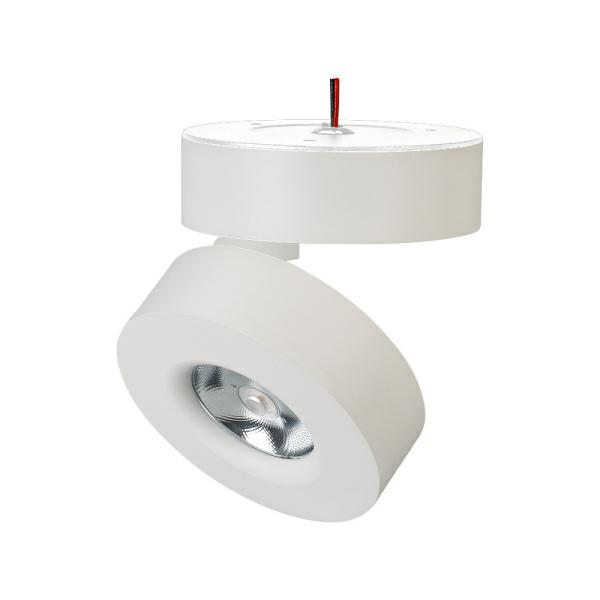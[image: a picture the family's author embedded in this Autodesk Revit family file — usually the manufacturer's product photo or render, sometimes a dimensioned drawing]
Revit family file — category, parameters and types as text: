
# Revit family: MONA-SURFACE
name_source: partatom
category: Осветительные приборы
revit_build: Autodesk Revit 2017 (Build: 20160225_1515(x64)
units: mm (PartAtom-declared; Revit-internal decimal feet)

## family parameters
Всегда вертикально = Да
Источник света = Нет
На основе рабочей плоскости = Нет
Общий = Нет
При загрузке вырезать с полостями = Нет
Размер круглого соединителя = Использовать диаметр
Тип детали = Нормальный
Точка расчета площади = Нет

## types (6) — shared parameters
ADSK_Единица измерения = шт.
ADSK_Завод-изготовитель = ARLIGHT
ADSK_Классификация нагрузок = Освещение
ADSK_Количество фаз = 1
ADSK_Количество фаз числовое = 1
ADSK_Коэффициент мощности = 0.53
ADSK_Масса_Текст = 0.674
ADSK_Наименование = Светильник
ADSK_Напряжение = 230 В
ADSK_Номинальная мощность = 12 Вт
ADSK_Полная мощность = 23 В·А
ADSK_Размер_Высота = 71 мм
ADSK_Размер_Диаметр = 100 мм
ADSK_Ток = 0 А
ARL_Драйвер = Встроенный (DC 300mA, 25-42V)
ARL_Индекс цветопередачи = >90
ARL_Класс защиты от поражения электрическим током = II
ARL_Класс пылевлагозащиты = IP40
ARL_Область использования = Для освещения в квартирах, офисах, музеях, магазинах с высокими требованиями к качеству света
ARL_Рабочая температура окружающей среды = -10...+50 °C
ARL_Серия = MONA
ARL_Способ монтажа = Накладной
ARL_Тип товара = Светильник
ARL_Угол обзора = 24°
URL = https://arlight.ru
Группа модели = Светильники
Изготовитель = ARLIGHT
Изготовитель (сайт) = www.arlight.ru
Изготовитель (телефон) = 8 800 505 26 29
Исходная интенсивность (лм) = 800
Полная установленная мощность = 23 В·А
Разработчик = НТЦ Конструктор
Разработчик (URL) = https://constructor.ru
Разработчик (телефон) = +7 (495) 781-05-35

## per-type parameters (varying)
| type | ADSK_Код изделия | ADSK_Марка | ARL_Материал корпуса | ARL_Обозначение корпуса | ARL_Цвет покрытия | ARL_Цвет свечения | Комментарии к типоразмеру | Описание | Фотометрия | Цветовая температура (К) |
| 025438 Светильник SP-MONA-SURFACE-R100-12W White5000 (WH, 24 deg) | Арт. 025438 | SP-MONA-SURFACE-R100-12W White5000 | Металл, белый | Корпус круглый, алюминий, цвет белый | Белый | Дневной 5000K | Арт. 025438 | Накладной откидной поворотный светильник 12 Вт. Цвет БЕЛЫЙ 5000K, св.поток 800лм, CRI(Ra)>90, угол свечения 24°, угол поворота 355°, угол наклона 90°. Корпус круглый, белый алюминий, IP40. Размер DxH Ø100x71 мм. Питание AC 220-240V, 12 Вт, драйвер встроенный (DC 300mA, 25-42V) | MONA-SURFACE IES Data : 025438_SP-MONA-SURFACE-R100-12W White5000 (WH, 24 deg) | 5000 |
| 025439 Светильник SP-MONA-SURFACE-R100-12W Day4000 (WH, 24 deg) | Арт. 025439 | SP-MONA-SURFACE-R100-12W Day4000 | Металл, белый | Корпус круглый, алюминий, цвет белый | Белый | Дневной 4000K | Арт. 025439 | Накладной откидной поворотный светильник 12 Вт. Цвет ДНЕВНОЙ 4000K, св.поток 800лм, CRI(Ra)>90, угол свечения 24°, угол поворота 355°, угол наклона 90°. Корпус круглый, белый алюминий, IP40. Размер DxH Ø100x71 мм. Питание AC 220-240V, 12 Вт, драйвер встроенный (DC 300mA, 25-42V) | MONA-SURFACE IES Data : 025439_SP-MONA-SURFACE-R100-12W Day4000 (WH, 24 deg) | 4000 |
| 025440 Светильник SP-MONA-SURFACE-R100-12W Warm3000 (WH, 24 deg) | Арт. 025440 | SP-MONA-SURFACE-R100-12W Warm3000 | Металл, белый | Корпус круглый, алюминий, цвет белый | Белый | Теплый 3000K | Арт. 025440 | Накладной откидной поворотный светильник 12 Вт. Цвет ТЕПЛЫЙ 3000K, св.поток 800лм, CRI(Ra)>90, угол свечения 24°, угол поворота 355°, угол наклона 90°. Корпус круглый, белый алюминий, IP40. Размер DxH Ø100x71 мм. Питание AC 220-240V, 12 Вт, драйвер встроенный (DC 300mA, 25-42V) | MONA-SURFACE IES Data : 025440_SP-MONA-SURFACE-R100-12W Warm3000 (WH, 24 deg) | 3000 |
| 025441 Светильник SP-MONA-SURFACE-R100-12W White5000 (BK, 24 deg) | Арт. 025441 | SP-MONA-SURFACE-R100-12W White5000 | Металл, чёрный | Корпус круглый, алюминий, цвет черный | Черный | Дневной 5000K | Арт. 025441 | Накладной откидной поворотный светильник 12 Вт. Цвет БЕЛЫЙ 5000K, св.поток 800лм, CRI(Ra)>90, угол свечения 24°, угол поворота 355°, угол наклона 90°. Корпус круглый, черный алюминий, IP40. Размер DxH Ø100x71 мм. Питание AC 220-240V, 12 Вт, драйвер встроенный (DC 300mA, 25-42V) | MONA-SURFACE IES Data : 025441_SP-MONA-SURFACE-R100-12W White5000 (BK, 24 deg) | 5000 |
| 025442 Светильник SP-MONA-SURFACE-R100-12W Day4000 (BK, 24 deg) | Арт. 025442 | SP-MONA-SURFACE-R100-12W Day4000 | Металл, чёрный | Корпус круглый, алюминий, цвет черный | Черный | Дневной 4000K | Арт. 025442 | Накладной откидной поворотный светильник 12 Вт. Цвет ДНЕВНОЙ 4000K, св.поток 800лм, CRI(Ra)>90, угол свечения 24°, угол поворота 355°, угол наклона 90°. Корпус круглый, черный алюминий, IP40. Размер DxH Ø100x71 мм. Питание AC 220-240V, 12 Вт, драйвер встроенный (DC 300mA, 25-42V) | MONA-SURFACE IES Data : 025442_SP-MONA-SURFACE-R100-12W Day4000 (BK, 24 deg) | 4000 |
| 025443 Светильник SP-MONA-SURFACE-R100-12W Warm3000 (BK, 24 deg) | Арт. 025443 | SP-MONA-SURFACE-R100-12W Warm3000 | Металл, чёрный | Корпус круглый, алюминий, цвет черный | Черный | Теплый 3000K | Арт. 025443 | Накладной откидной поворотный светильник 12 Вт. Цвет ТЕПЛЫЙ 3000K, св.поток 800лм, CRI(Ra)>90, угол свечения 24°, угол поворота 355°, угол наклона 90°. Корпус круглый, черный алюминий, IP40. Размер DxH Ø100x71 мм. Питание AC 220-240V, 12 Вт, драйвер встроенный (DC 300mA, 25-42V) | MONA-SURFACE IES Data : 025443_SP-MONA-SURFACE-R100-12W Warm3000 (BK, 24 deg) | 3000 |

## geometry (parser evidence)
native form markers: Sweep x3
no freeform markers — native parametric forms only
